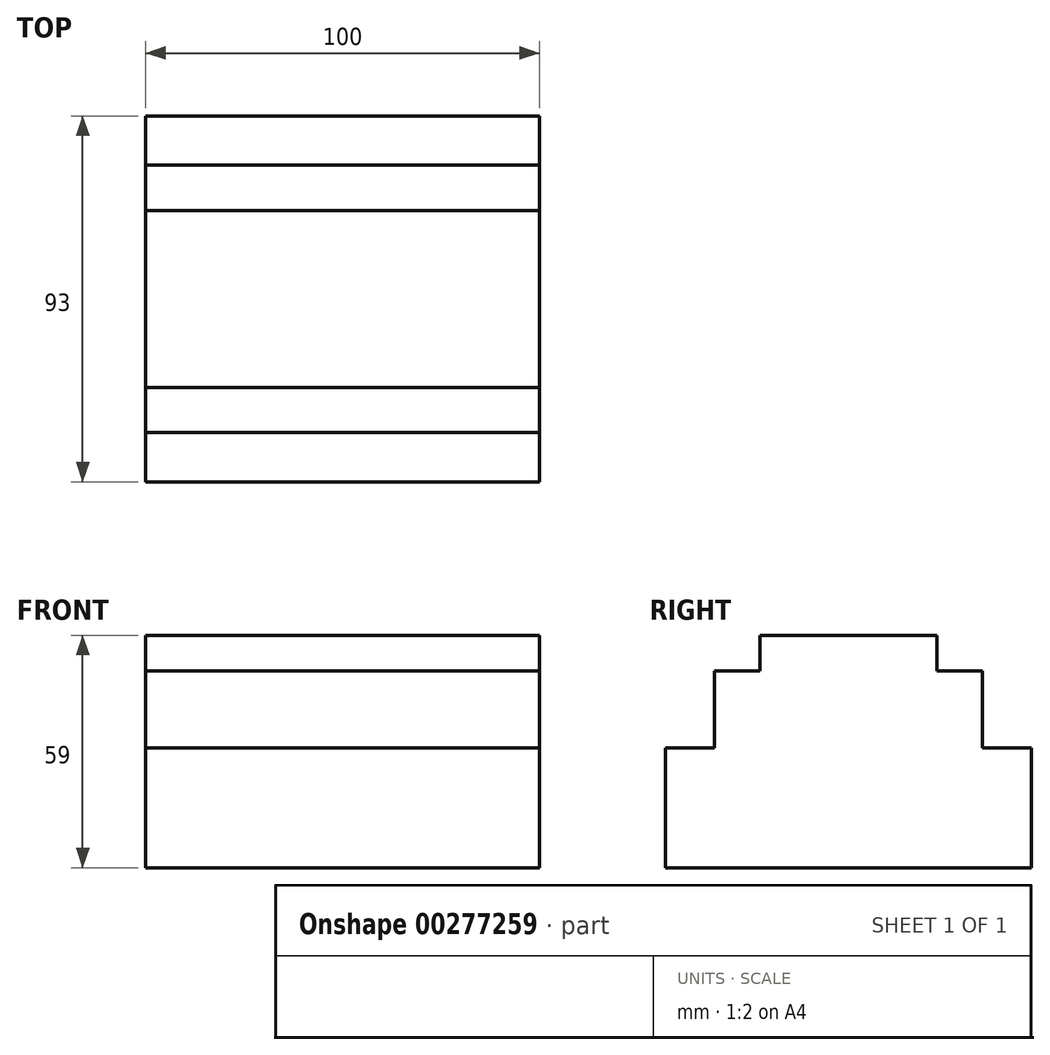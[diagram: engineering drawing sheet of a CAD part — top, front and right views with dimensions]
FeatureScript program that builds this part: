
annotation { "Feature Type Name" : "Feature", "Feature Type Description" : "" }
export const myFeature = defineFeature(function(context is Context, id is Id, definition is map)
    precondition{}
    {
        {
            var Q0;
            Q0=qCreatedBy(makeId("Top.planeOp"),FACE);
            var sketch = newSketch(context, id + "F0", { "sketchPlane" : qUnion([Q0])});
            skLineSegment(sketch, "E0.bottom", {"start": v(50, -22.5) * mm, "end": v(-50, -22.5) * mm});
            skLineSegment(sketch, "E0.top", {"start": v(50, 22.5) * mm, "end": v(-50, 22.5) * mm});
            skLineSegment(sketch, "E0.left", {"start": v(50, -22.5) * mm, "end": v(50, 22.5) * mm});
            skLineSegment(sketch, "E0.right", {"start": v(-50, -22.5) * mm, "end": v(-50, 22.5) * mm});
            skPoint(sketch, "E0.middle", {"position": v(0, 0) * mm});
            skLineSegment(sketch, "E1.bottom", {"start": v(50, -34) * mm, "end": v(-50, -34) * mm});
            skLineSegment(sketch, "E1.top", {"start": v(50, 34) * mm, "end": v(-50, 34) * mm});
            skLineSegment(sketch, "E1.left", {"start": v(50, -34) * mm, "end": v(50, 34) * mm});
            skLineSegment(sketch, "E1.right", {"start": v(-50, -34) * mm, "end": v(-50, 34) * mm});
            skLineSegment(sketch, "E2.bottom", {"start": v(50, -46.5) * mm, "end": v(-50, -46.5) * mm});
            skLineSegment(sketch, "E2.top", {"start": v(50, 46.5) * mm, "end": v(-50, 46.5) * mm});
            skLineSegment(sketch, "E2.left", {"start": v(50, -46.5) * mm, "end": v(50, 46.5) * mm});
            skLineSegment(sketch, "E2.right", {"start": v(-50, -46.5) * mm, "end": v(-50, 46.5) * mm});
            skSolve(sketch);
        }
        {
            var Q0;
            {var subQ0=sQuery(id+"F0.wireOp",EDGE,"E0.bottom");Q0=makeQuery(id+"F0.imprint","IMPRINT",FACE,{"disambiguationData":[TD([[makeQuery(id+"F0.imprint","IMPRINT",EDGE,{"derivedFrom":subQ0}),-1.0]])]});}
            extrude(context, id + "F1", {"entities" : qUnion([Q0]), "depth" : 59 * mm});
        }
        {
            var Q0;
            {var subQ0=sQuery(id+"F0.wireOp",EDGE,"E0.top");Q0=makeQuery(id+"F0.imprint","IMPRINT",FACE,{"disambiguationData":[TD([[makeQuery(id+"F0.imprint","IMPRINT",EDGE,{"derivedFrom":subQ0}),-1.0]])]});}
            var Q1;
            {var subQ0=sQuery(id+"F0.wireOp",EDGE,"E0.bottom");Q1=makeQuery(id+"F0.imprint","IMPRINT",FACE,{"disambiguationData":[TD([[makeQuery(id+"F0.imprint","IMPRINT",EDGE,{"derivedFrom":subQ0}),1.0]])]});}
            extrude(context, id + "F2", {"entities" : qUnion([Q0, Q1]), "operationType" : NewBodyOperationType.ADD, "depth" : 50 * mm});
        }
        {
            var Q0;
            {var subQ0=sQuery(id+"F0.wireOp",EDGE,"E1.top");Q0=makeQuery(id+"F0.imprint","IMPRINT",FACE,{"disambiguationData":[TD([[makeQuery(id+"F0.imprint","IMPRINT",EDGE,{"derivedFrom":subQ0}),-1.0]])]});}
            var Q1;
            {var subQ0=sQuery(id+"F0.wireOp",EDGE,"E1.bottom");Q1=makeQuery(id+"F0.imprint","IMPRINT",FACE,{"disambiguationData":[TD([[makeQuery(id+"F0.imprint","IMPRINT",EDGE,{"derivedFrom":subQ0}),1.0]])]});}
            extrude(context, id + "F3", {"entities" : qUnion([Q0, Q1]), "operationType" : NewBodyOperationType.ADD, "depth" : 30.4 * mm});
        }
    });
